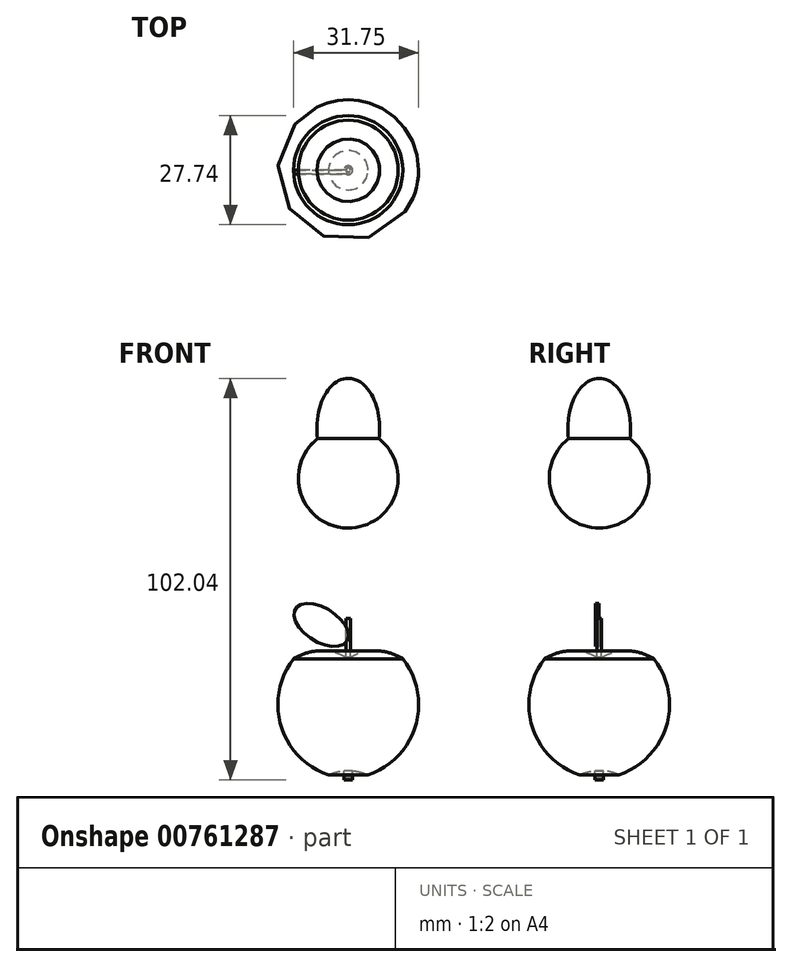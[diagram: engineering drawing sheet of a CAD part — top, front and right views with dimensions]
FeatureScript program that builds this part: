
annotation { "Feature Type Name" : "Feature", "Feature Type Description" : "" }
export const myFeature = defineFeature(function(context is Context, id is Id, definition is map)
    precondition{}
    {
        {
            var Q0;
            Q0=qCreatedBy(makeId("Front.planeOp"),FACE);
            var sketch = newSketch(context, id + "F0", { "sketchPlane" : qUnion([Q0])});
            skArc(sketch, "E0", {"start": v(-0.52, 0.31) * mm, "mid": v(-7.23, 2) * mm, "end": v(-13.87, 0) * mm});
            skArc(sketch, "E1", {"start": v(-1.11, -28.44) * mm, "mid": v(-3.1, -28.8) * mm, "end": v(-5, -29.49) * mm});
            skArc(sketch, "E2", {"start": v(-13.87, 0) * mm, "mid": v(-17.08, -17.04) * mm, "end": v(-5, -29.49) * mm});
            skLineSegment(sketch, "E3", {"start": v(-0.52, 0.31) * mm, "end": v(-0.52, 5.36) * mm});
            skLineSegment(sketch, "E4", {"start": v(-1.11, -28.44) * mm, "end": v(-1.11, -30.77) * mm});
            skLineSegment(sketch, "E5", {"start": v(-1.11, -30.77) * mm, "end": v(-0.61, -30.18) * mm});
            skLineSegment(sketch, "E6", {"start": v(-0.61, -30.18) * mm, "end": v(0, -30.7) * mm});
            skLineSegment(sketch, "E7", {"start": v(0, -30.7) * mm, "end": v(0, -28.38) * mm});
            skLineSegment(sketch, "E8", {"start": v(0, 5.36) * mm, "end": v(0, -28.38) * mm});
            skLineSegment(sketch, "E9", {"start": v(-0.52, 5.36) * mm, "end": v(-0.52, 10.31) * mm});
            skLineSegment(sketch, "E10", {"start": v(-0.52, 10.31) * mm, "end": v(0, 10.31) * mm});
            skLineSegment(sketch, "E11", {"start": v(0, 10.31) * mm, "end": v(0, 5.36) * mm});
            skSolve(sketch);
        }
        {
            var Q0;
            Q0=makeQuery(id+"F0.imprint","IMPRINT",FACE,{"disambiguationData":[TD([[makeQuery(id+"F0.imprint","IMPRINT",EDGE,{"derivedFrom":sQuery(id+"F0.wireOp",EDGE,"E0")}),1.0]])]});
            var Q1;
            Q1=sQuery(id+"F0.wireOp",EDGE,"E8");
            revolve(context, id + "F1", {"surfaceOperationType" : NewSurfaceOperationType.NEW, "entities" : qUnion([Q0]), "axis" : qUnion([Q1]), "revolveType" : RevolveType.FULL});
        }
        {
            var Q0;
            Q0=qCreatedBy(makeId("Front.planeOp"),FACE);
            var sketch = newSketch(context, id + "F2", { "sketchPlane" : qUnion([Q0])});
            skEllipse(sketch, "E12", {"center": v(-6.88, 8.6) * mm, "majorRadius": 7.7 * mm, "minorRadius": 4.29 * mm, "majorAxis": v(0.85, -0.53)});
            skSolve(sketch);
        }
        {
            var Q0;
            Q0=makeQuery(id+"F2.imprint","IMPRINT",FACE,{"disambiguationData":[TD([[makeQuery(id+"F2.imprint","IMPRINT",EDGE,{"derivedFrom":sQuery(id+"F2.wireOp",EDGE,"E12")}),1.0]])]});
            extrude(context, id + "F3", {"entities" : qUnion([Q0]), "operationType" : NewBodyOperationType.ADD, "depth" : 1 * mm, "offsetDistance" : 25 * mm});
        }
        {
            var Q0;
            Q0=qCreatedBy(makeId("Front.planeOp"),FACE);
            var sketch = newSketch(context, id + "F4", { "sketchPlane" : qUnion([Q0])});
            skArc(sketch, "E13", {"start": v(-7.79, 55.91) * mm, "mid": v(-12, 41.78) * mm, "end": v(0, 33.22) * mm});
            skEllipticalArc(sketch, "E14", {});
            skLineSegment(sketch, "E15", {"start": v(0, 71.27) * mm, "end": v(0, 33.22) * mm});
            const initialGuessF4  = {"E14": [0, 0.05858651481932946, 0, -1, 0.012685510594313817, 0.00796629098158652, 3.141592653589793, 4.924592121919469]};
            skSetInitialGuess(sketch, initialGuessF4);
            skSolve(sketch);
        }
        {
            var Q0;
            Q0=makeQuery(id+"F4.imprint","IMPRINT",FACE,{"disambiguationData":[TD([[makeQuery(id+"F4.imprint","IMPRINT",EDGE,{"derivedFrom":sQuery(id+"F4.wireOp",EDGE,"E13")}),1.0]])]});
            var Q1;
            Q1=sQuery(id+"F4.wireOp",EDGE,"E15");
            revolve(context, id + "F5", {"surfaceOperationType" : NewSurfaceOperationType.NEW, "entities" : qUnion([Q0]), "axis" : qUnion([Q1]), "revolveType" : RevolveType.FULL});
        }
    });
